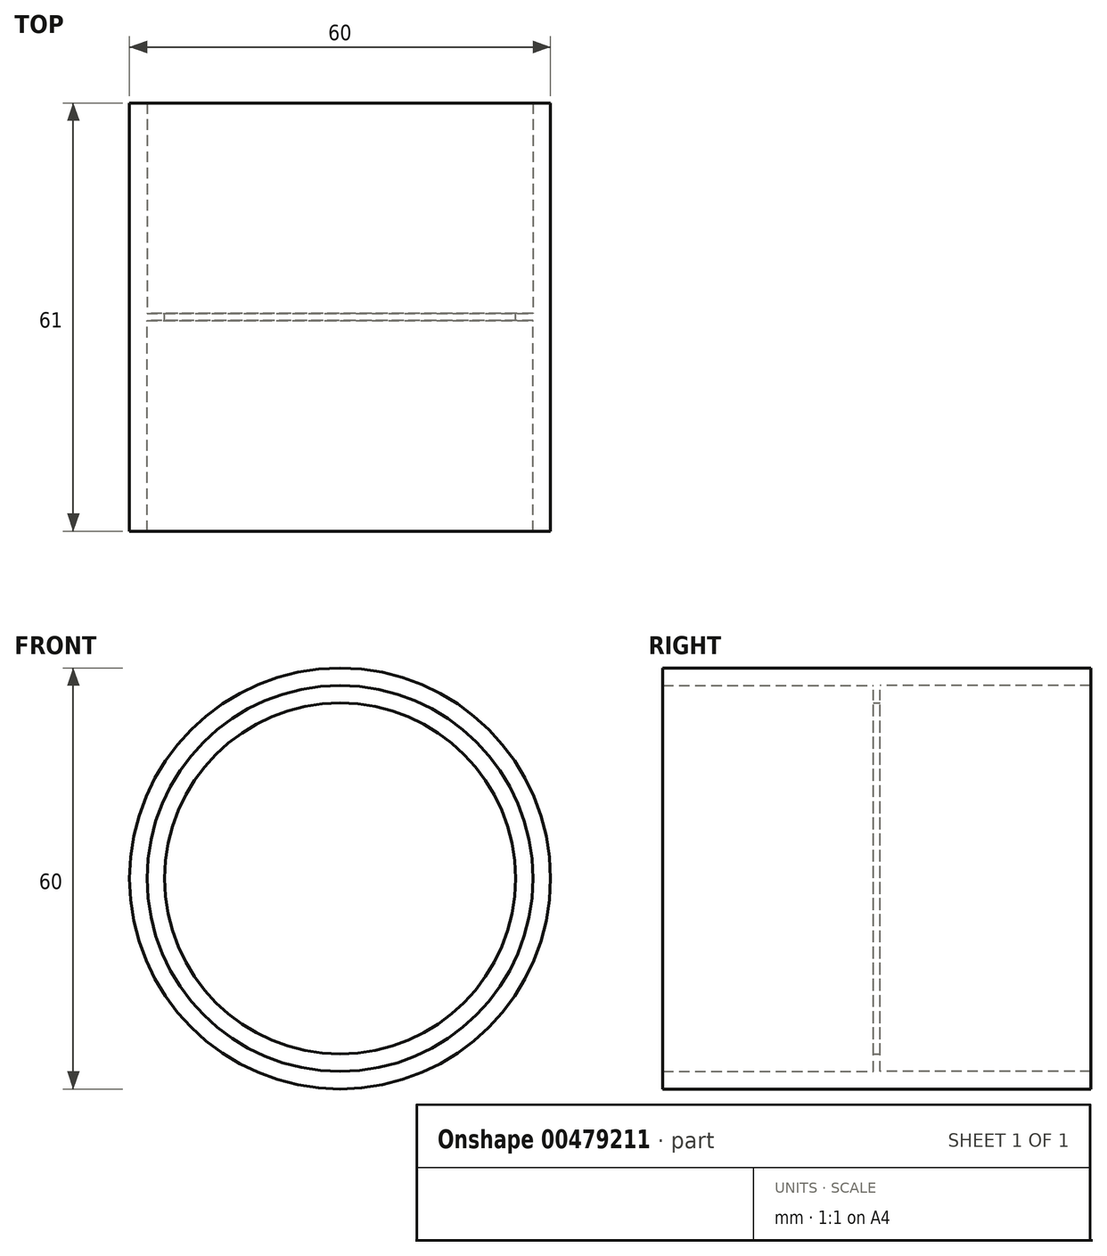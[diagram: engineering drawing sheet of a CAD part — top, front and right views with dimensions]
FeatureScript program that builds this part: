
annotation { "Feature Type Name" : "Feature", "Feature Type Description" : "" }
export const myFeature = defineFeature(function(context is Context, id is Id, definition is map)
    precondition{}
    {
        {
            var Q0;
            Q0=qCreatedBy(makeId("Front.planeOp"),FACE);
            var sketch = newSketch(context, id + "F0", { "sketchPlane" : qUnion([Q0])});
            skCircle(sketch, "E0", {"center": v(0, 0) * mm, "radius": 30 * mm});
            skCircle(sketch, "E1", {"center": v(0, 0) * mm, "radius": 27.5 * mm});
            skCircle(sketch, "E2", {"center": v(0, 0) * mm, "radius": 25 * mm});
            skSolve(sketch);
        }
        {
            var Q0;
            Q0=makeQuery(id+"F0.imprint","IMPRINT",FACE,{"disambiguationData":[TD([[makeQuery(id+"F0.imprint","IMPRINT",EDGE,{"derivedFrom":sQuery(id+"F0.wireOp",EDGE,"E0")}),1.0]])]});
            extrude(context, id + "F1", {"entities" : qUnion([Q0]), "depth" : 31 * mm});
        }
        {
            var Q0;
            Q0=makeQuery(id+"F0.imprint","IMPRINT",FACE,{"disambiguationData":[TD([[makeQuery(id+"F0.imprint","IMPRINT",EDGE,{"derivedFrom":sQuery(id+"F0.wireOp",EDGE,"E1")}),1.0]])]});
            extrude(context, id + "F2", {"entities" : qUnion([Q0]), "operationType" : NewBodyOperationType.ADD, "depth" : 1 * mm});
        }
        {
            var Q0;
            Q0=makeQuery(id+"F0.imprint","IMPRINT",FACE,{"disambiguationData":[TD([[makeQuery(id+"F0.imprint","IMPRINT",EDGE,{"derivedFrom":sQuery(id+"F0.wireOp",EDGE,"E0")}),1.0]])]});
            extrude(context, id + "F3", {"entities" : qUnion([Q0]), "operationType" : NewBodyOperationType.ADD, "oppositeDirection" : true, "depth" : 30 * mm});
        }
    });
